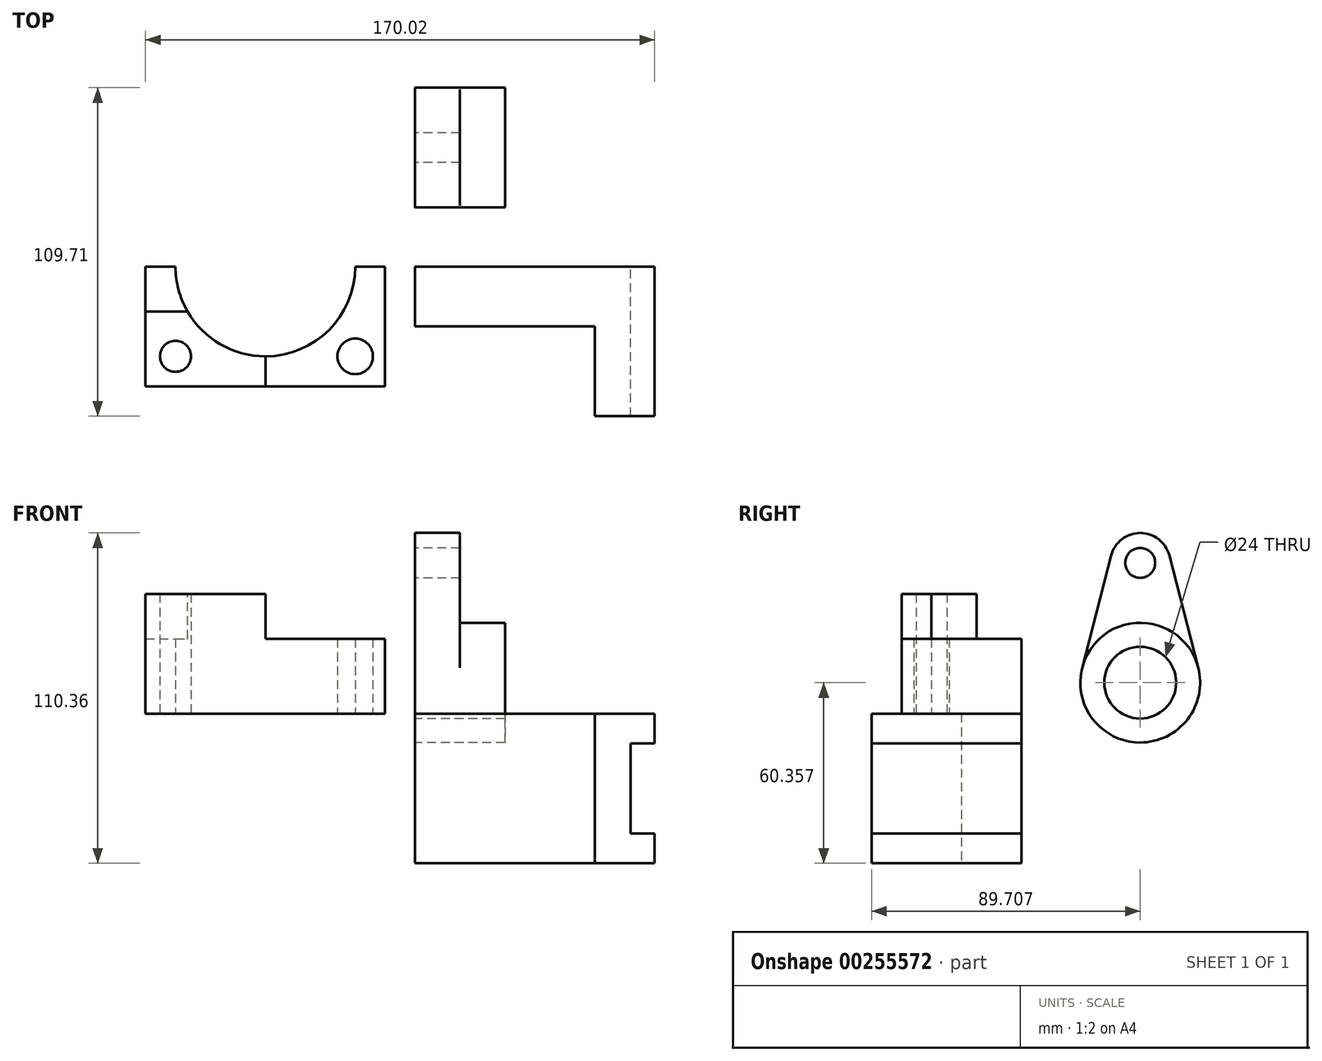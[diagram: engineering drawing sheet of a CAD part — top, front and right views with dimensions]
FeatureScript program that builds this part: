
annotation { "Feature Type Name" : "Feature", "Feature Type Description" : "" }
export const myFeature = defineFeature(function(context is Context, id is Id, definition is map)
    precondition{}
    {
        {
            var Q0;
            Q0=qCreatedBy(makeId("Front.planeOp"),FACE);
            var sketch = newSketch(context, id + "F0", { "sketchPlane" : qUnion([Q0])});
            skLineSegment(sketch, "E0.bottom", {"start": v(0, 0) * mm, "end": v(60, 0) * mm});
            skLineSegment(sketch, "E0.top", {"start": v(0, -50) * mm, "end": v(60, -50) * mm});
            skLineSegment(sketch, "E0.left", {"start": v(0, 0) * mm, "end": v(0, -50) * mm});
            skLineSegment(sketch, "E0.right", {"start": v(60, 0) * mm, "end": v(60, -50) * mm});
            skLineSegment(sketch, "E1.bottom", {"start": v(60, 0) * mm, "end": v(80, 0) * mm});
            skLineSegment(sketch, "E1.top", {"start": v(60, -50) * mm, "end": v(80, -50) * mm});
            skLineSegment(sketch, "E1.right", {"start": v(80, 0) * mm, "end": v(80, -50) * mm});
            skLineSegment(sketch, "E2.bottom", {"start": v(80, -10) * mm, "end": v(72, -10) * mm});
            skLineSegment(sketch, "E2.top", {"start": v(80, -40) * mm, "end": v(72, -40) * mm});
            skLineSegment(sketch, "E2.left", {"start": v(80, -10) * mm, "end": v(80, -40) * mm});
            skLineSegment(sketch, "E2.right", {"start": v(72, -10) * mm, "end": v(72, -40) * mm});
            skSolve(sketch);
        }
        {
            var Q0;
            Q0=makeQuery(id+"F0.imprint","IMPRINT",FACE,{"disambiguationData":[TD([[makeQuery(id+"F0.imprint","IMPRINT",EDGE,{"derivedFrom":sQuery(id+"F0.wireOp",EDGE,"E0.bottom")}),-1.0]])]});
            extrude(context, id + "F1", {"entities" : qUnion([Q0]), "depth" : 20 * mm});
        }
        {
            var Q0;
            {var subQ1=sQuery(id+"F0.wireOp",EDGE,"E1.bottom");Q0=makeQuery(id+"F0.imprint","IMPRINT",FACE,{"disambiguationData":[TD([[makeQuery(id+"F0.imprint","IMPRINT",EDGE,{"derivedFrom":subQ1}),-1.0]])]});}
            extrude(context, id + "F2", {"entities" : qUnion([Q0]), "operationType" : NewBodyOperationType.ADD, "depth" : 50 * mm});
        }
        {
            var Q0;
            Q0=qCreatedBy(makeId("Right.planeOp"),FACE);
            var sketch = newSketch(context, id + "F3", { "sketchPlane" : qUnion([Q0])});
            skCircle(sketch, "E3", {"center": v(39.7, 10.36) * mm, "radius": 12 * mm});
            skCircle(sketch, "E4", {"center": v(39.7, 10.36) * mm, "radius": 20 * mm});
            skCircle(sketch, "E5", {"center": v(39.7, 50.36) * mm, "radius": 5 * mm});
            skArc(sketch, "E6", {"start": v(49.39, 52.86) * mm, "mid": v(39.7, 60.36) * mm, "end": v(30.02, 52.86) * mm});
            skLineSegment(sketch, "E7", {"start": v(20.34, 15.36) * mm, "end": v(30.02, 52.86) * mm});
            skLineSegment(sketch, "E8", {"start": v(59.07, 15.36) * mm, "end": v(49.39, 52.86) * mm});
            skSolve(sketch);
        }
        {
            var Q0;
            Q0=makeQuery(id+"F3.imprint","IMPRINT",FACE,{"disambiguationData":[TD([[makeQuery(id+"F3.imprint","IMPRINT",EDGE,{"derivedFrom":sQuery(id+"F3.wireOp",EDGE,"E3")}),-1.0]])]});
            extrude(context, id + "F4", {"entities" : qUnion([Q0]), "depth" : 30 * mm});
        }
        {
            var Q0;
            Q0=makeQuery(id+"F3.imprint","IMPRINT",FACE,{"disambiguationData":[TD([[makeQuery(id+"F3.imprint","IMPRINT",EDGE,{"derivedFrom":sQuery(id+"F3.wireOp",EDGE,"E5")}),-1.0]])]});
            extrude(context, id + "F5", {"entities" : qUnion([Q0]), "operationType" : NewBodyOperationType.ADD, "depth" : 15 * mm});
        }
        {
            var Q0;
            Q0=qCreatedBy(makeId("Top.planeOp"),FACE);
            var sketch = newSketch(context, id + "F6", { "sketchPlane" : qUnion([Q0])});
            skLineSegment(sketch, "E9.bottom", {"start": v(-90.02, 0) * mm, "end": v(-80.02, 0) * mm});
            skLineSegment(sketch, "E9.top", {"start": v(-90.02, -40) * mm, "end": v(-10.02, -40) * mm});
            skLineSegment(sketch, "E9.left", {"start": v(-90.02, 0) * mm, "end": v(-90.02, -40) * mm});
            skLineSegment(sketch, "E9.right", {"start": v(-10.02, 0) * mm, "end": v(-10.02, -40) * mm});
            skArc(sketch, "E10", {"start": v(-80.02, 0) * mm, "mid": v(-50.02, -30) * mm, "end": v(-20.02, 0) * mm});
            skLineSegment(sketch, "E11.trimOffspring", {"start": v(-20.02, 0) * mm, "end": v(-10.02, 0) * mm});
            skCircle(sketch, "E12", {"center": v(-80.02, -30) * mm, "radius": 5.18 * mm});
            skCircle(sketch, "E13", {"center": v(-20.02, -30) * mm, "radius": 5.94 * mm});
            skSolve(sketch);
        }
        {
            var Q0;
            Q0=makeQuery(id+"F6.imprint","IMPRINT",FACE,{"disambiguationData":[TD([[makeQuery(id+"F6.imprint","IMPRINT",EDGE,{"derivedFrom":sQuery(id+"F6.wireOp",EDGE,"E9.bottom")}),-1.0]])]});
            extrude(context, id + "F7", {"entities" : qUnion([Q0]), "depth" : 40 * mm});
        }
        {
            var Q0;
            Q0=makeQuery(id+"F7.opExtrude","CAP_FACE",FACE,{"disambiguationData":[OSD([sQuery(id+"F6.wireOp",EDGE,"E9.bottom"),sQuery(id+"F6.wireOp",EDGE,"E9.top"),sQuery(id+"F6.wireOp",EDGE,"E9.left"),sQuery(id+"F6.wireOp",EDGE,"E9.right"),sQuery(id+"F6.wireOp",EDGE,"E10"),sQuery(id+"F6.wireOp",EDGE,"E11.trimOffspring"),sQuery(id+"F6.wireOp",EDGE,"E12"),sQuery(id+"F6.wireOp",EDGE,"E13")])],"isStart":false});
            var sketch = newSketch(context, id + "F8", { "sketchPlane" : qUnion([Q0])});
            skLineSegment(sketch, "E14.bottom", {"start": v(-103.53, 13.37) * mm, "end": v(-65.39, 13.37) * mm});
            skLineSegment(sketch, "E14.top", {"start": v(-103.53, -15) * mm, "end": v(-65.39, -15) * mm});
            skLineSegment(sketch, "E14.left", {"start": v(-103.53, 13.37) * mm, "end": v(-103.53, -15) * mm});
            skLineSegment(sketch, "E14.right", {"start": v(-65.39, 13.37) * mm, "end": v(-65.39, -15) * mm});
            skLineSegment(sketch, "E15", {"start": v(-50.02, -30) * mm, "end": v(-50.02, -40) * mm});
            skSolve(sketch);
        }
        {
            var Q0;
            {var subQ5=makeQuery(id+"F7.opExtrude","CAP_EDGE",EDGE,{"disambiguationData":[OSD([sQuery(id+"F6.wireOp",EDGE,"E9.bottom")])],"isStart":false});Q0=makeQuery(id+"F8.imprint","IMPRINT",FACE,{"disambiguationData":[TD([[makeQuery(id+"F8.imprint","IMPRINT",EDGE,{"derivedFrom":subQ5}),-1.0]])]});}
            var Q1;
            {var subQ2=sQuery(id+"F8.wireOp",EDGE,"E15");Q1=makeQuery(id+"F8.imprint","IMPRINT",FACE,{"disambiguationData":[TD([[makeQuery(id+"F8.imprint","IMPRINT",EDGE,{"derivedFrom":subQ2}),1.0]])]});}
            extrude(context, id + "F9", {"entities" : qUnion([Q0, Q1]), "operationType" : NewBodyOperationType.REMOVE, "oppositeDirection" : true, "depth" : 15 * mm});
        }
    });
